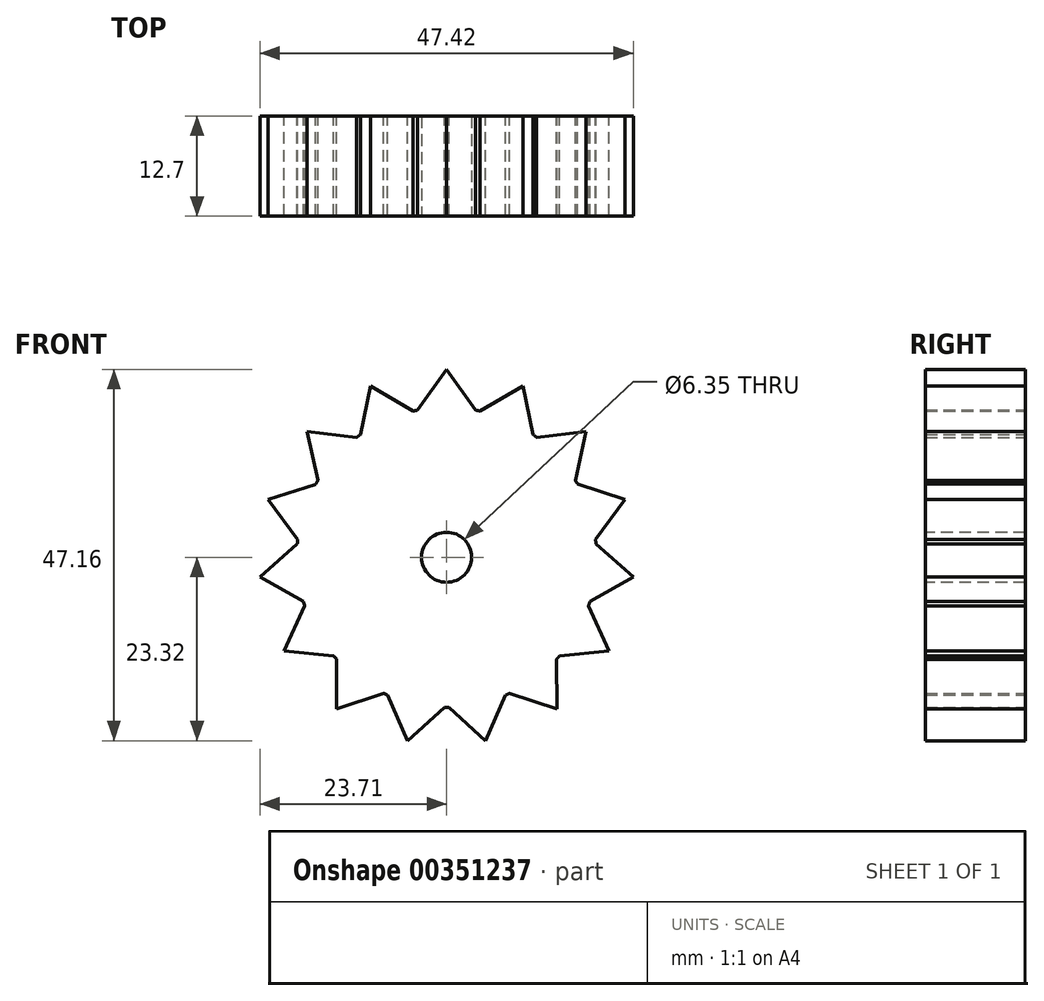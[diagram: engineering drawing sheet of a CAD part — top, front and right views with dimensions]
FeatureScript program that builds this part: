
annotation { "Feature Type Name" : "Feature", "Feature Type Description" : "" }
export const myFeature = defineFeature(function(context is Context, id is Id, definition is map)
    precondition{}
    {
        {
            var Q0;
            Q0=qCreatedBy(makeId("Front.planeOp"),FACE);
            var sketch = newSketch(context, id + "F0", { "sketchPlane" : qUnion([Q0])});
            skCircle(sketch, "E0", {"center": v(0, 0) * mm, "radius": 19.05 * mm});
            skPoint(sketch, "E1.start.orphan", {"position": v(0, 19.05) * mm});
            skLineSegment(sketch, "E2", {"start": v(0, 23.84) * mm, "end": v(3.68, 18.7) * mm});
            skLineSegment(sketch, "E3", {"start": v(0, 23.84) * mm, "end": v(-3.68, 18.7) * mm});
            skLineSegment(sketch, "E4.1.0", {"start": v(-9.7, 21.77) * mm, "end": v(-10.96, 15.58) * mm});
            skLineSegment(sketch, "E4.1.1", {"start": v(-9.7, 21.77) * mm, "end": v(-4.24, 18.57) * mm});
            skLineSegment(sketch, "E4.2.0", {"start": v(-17.71, 15.95) * mm, "end": v(-16.35, 9.77) * mm});
            skLineSegment(sketch, "E4.2.1", {"start": v(-17.71, 15.95) * mm, "end": v(-11.43, 15.24) * mm});
            skLineSegment(sketch, "E4.3.0", {"start": v(-22.67, 7.36) * mm, "end": v(-18.91, 2.28) * mm});
            skLineSegment(sketch, "E4.3.1", {"start": v(-22.67, 7.36) * mm, "end": v(-16.64, 9.27) * mm});
            skLineSegment(sketch, "E4.4.0", {"start": v(-23.7, -2.5) * mm, "end": v(-18.2, -5.61) * mm});
            skLineSegment(sketch, "E4.4.1", {"start": v(-23.7, -2.5) * mm, "end": v(-18.97, 1.7) * mm});
            skLineSegment(sketch, "E4.5.0", {"start": v(-20.64, -11.92) * mm, "end": v(-14.35, -12.53) * mm});
            skLineSegment(sketch, "E4.5.1", {"start": v(-20.64, -11.92) * mm, "end": v(-18.03, -6.16) * mm});
            skLineSegment(sketch, "E4.6.0", {"start": v(-14, -19.28) * mm, "end": v(-8, -17.28) * mm});
            skLineSegment(sketch, "E4.6.1", {"start": v(-14, -19.28) * mm, "end": v(-13.96, -12.96) * mm});
            skLineSegment(sketch, "E4.7.0", {"start": v(-4.95, -23.32) * mm, "end": v(-0.29, -19.05) * mm});
            skLineSegment(sketch, "E4.7.1", {"start": v(-4.95, -23.32) * mm, "end": v(-7.48, -17.52) * mm});
            skLineSegment(sketch, "E4.8.0", {"start": v(4.96, -23.31) * mm, "end": v(7.49, -17.52) * mm});
            skLineSegment(sketch, "E4.8.1", {"start": v(4.96, -23.31) * mm, "end": v(0.29, -19.05) * mm});
            skLineSegment(sketch, "E4.9.0", {"start": v(14.01, -19.28) * mm, "end": v(13.96, -12.96) * mm});
            skLineSegment(sketch, "E4.9.1", {"start": v(14.01, -19.28) * mm, "end": v(8.01, -17.28) * mm});
            skLineSegment(sketch, "E4.10.0", {"start": v(20.64, -11.92) * mm, "end": v(18.03, -6.16) * mm});
            skLineSegment(sketch, "E4.10.1", {"start": v(20.64, -11.92) * mm, "end": v(14.35, -12.53) * mm});
            skLineSegment(sketch, "E4.11.0", {"start": v(23.7, -2.5) * mm, "end": v(18.97, 1.7) * mm});
            skLineSegment(sketch, "E4.11.1", {"start": v(23.7, -2.5) * mm, "end": v(18.2, -5.61) * mm});
            skLineSegment(sketch, "E4.12.0", {"start": v(22.67, 7.37) * mm, "end": v(16.64, 9.28) * mm});
            skLineSegment(sketch, "E4.12.1", {"start": v(22.67, 7.37) * mm, "end": v(18.91, 2.28) * mm});
            skLineSegment(sketch, "E4.13.0", {"start": v(17.71, 15.95) * mm, "end": v(11.43, 15.24) * mm});
            skLineSegment(sketch, "E4.13.1", {"start": v(17.71, 15.95) * mm, "end": v(16.35, 9.77) * mm});
            skLineSegment(sketch, "E4.14.0", {"start": v(9.7, 21.78) * mm, "end": v(4.24, 18.57) * mm});
            skLineSegment(sketch, "E4.14.1", {"start": v(9.7, 21.78) * mm, "end": v(10.96, 15.58) * mm});
            skSolve(sketch);
        }
        {
            var Q0;
            {var subQ0=sQuery(id+"F0.wireOp",EDGE,"E3");Q0=makeQuery(id+"F0.imprint","IMPRINT",FACE,{"disambiguationData":[TD([[makeQuery(id+"F0.imprint","IMPRINT",EDGE,{"derivedFrom":subQ0}),1.0]])]});}
            var Q1;
            {var subQ0=sQuery(id+"F0.wireOp",EDGE,"E4.1.0");Q1=makeQuery(id+"F0.imprint","IMPRINT",FACE,{"disambiguationData":[TD([[makeQuery(id+"F0.imprint","IMPRINT",EDGE,{"derivedFrom":subQ0}),1.0]])]});}
            var Q2;
            {var subQ0=sQuery(id+"F0.wireOp",EDGE,"E4.2.0");Q2=makeQuery(id+"F0.imprint","IMPRINT",FACE,{"disambiguationData":[TD([[makeQuery(id+"F0.imprint","IMPRINT",EDGE,{"derivedFrom":subQ0}),1.0]])]});}
            var Q3;
            {var subQ0=sQuery(id+"F0.wireOp",EDGE,"E4.3.0");Q3=makeQuery(id+"F0.imprint","IMPRINT",FACE,{"disambiguationData":[TD([[makeQuery(id+"F0.imprint","IMPRINT",EDGE,{"derivedFrom":subQ0}),1.0]])]});}
            var Q4;
            {var subQ0=sQuery(id+"F0.wireOp",EDGE,"E4.14.0");Q4=makeQuery(id+"F0.imprint","IMPRINT",FACE,{"disambiguationData":[TD([[makeQuery(id+"F0.imprint","IMPRINT",EDGE,{"derivedFrom":subQ0}),1.0]])]});}
            var Q5;
            {var subQ0=sQuery(id+"F0.wireOp",EDGE,"E4.13.0");Q5=makeQuery(id+"F0.imprint","IMPRINT",FACE,{"disambiguationData":[TD([[makeQuery(id+"F0.imprint","IMPRINT",EDGE,{"derivedFrom":subQ0}),1.0]])]});}
            var Q6;
            {var subQ0=sQuery(id+"F0.wireOp",EDGE,"E4.12.0");Q6=makeQuery(id+"F0.imprint","IMPRINT",FACE,{"disambiguationData":[TD([[makeQuery(id+"F0.imprint","IMPRINT",EDGE,{"derivedFrom":subQ0}),1.0]])]});}
            var Q7;
            {var subQ0=sQuery(id+"F0.wireOp",EDGE,"E4.11.0");Q7=makeQuery(id+"F0.imprint","IMPRINT",FACE,{"disambiguationData":[TD([[makeQuery(id+"F0.imprint","IMPRINT",EDGE,{"derivedFrom":subQ0}),1.0]])]});}
            var Q8;
            {var subQ0=sQuery(id+"F0.wireOp",EDGE,"E4.10.0");Q8=makeQuery(id+"F0.imprint","IMPRINT",FACE,{"disambiguationData":[TD([[makeQuery(id+"F0.imprint","IMPRINT",EDGE,{"derivedFrom":subQ0}),1.0]])]});}
            var Q9;
            {var subQ0=sQuery(id+"F0.wireOp",EDGE,"E4.9.0");Q9=makeQuery(id+"F0.imprint","IMPRINT",FACE,{"disambiguationData":[TD([[makeQuery(id+"F0.imprint","IMPRINT",EDGE,{"derivedFrom":subQ0}),1.0]])]});}
            var Q10;
            {var subQ0=sQuery(id+"F0.wireOp",EDGE,"E0");var subQ18=makeQuery(id+"F0.imprint","INTERSECT",VERTEX,{"derivedFrom":[subQ0,sQuery(id+"F0.wireOp",EDGE,"E4.11.0")]});Q10=makeQuery(id+"F0.imprint","IMPRINT",FACE,{"disambiguationData":[TD([[makeQuery(id+"F0.imprint","IMPRINT",EDGE,{"disambiguationData":[TD([[subQ18,-1.0]])],"derivedFrom":subQ0}),1.0]])]});}
            var Q11;
            {var subQ0=sQuery(id+"F0.wireOp",EDGE,"E4.8.0");Q11=makeQuery(id+"F0.imprint","IMPRINT",FACE,{"disambiguationData":[TD([[makeQuery(id+"F0.imprint","IMPRINT",EDGE,{"derivedFrom":subQ0}),1.0]])]});}
            var Q12;
            {var subQ0=sQuery(id+"F0.wireOp",EDGE,"E4.7.0");Q12=makeQuery(id+"F0.imprint","IMPRINT",FACE,{"disambiguationData":[TD([[makeQuery(id+"F0.imprint","IMPRINT",EDGE,{"derivedFrom":subQ0}),1.0]])]});}
            var Q13;
            {var subQ0=sQuery(id+"F0.wireOp",EDGE,"E4.6.0");Q13=makeQuery(id+"F0.imprint","IMPRINT",FACE,{"disambiguationData":[TD([[makeQuery(id+"F0.imprint","IMPRINT",EDGE,{"derivedFrom":subQ0}),1.0]])]});}
            var Q14;
            {var subQ0=sQuery(id+"F0.wireOp",EDGE,"E4.5.0");Q14=makeQuery(id+"F0.imprint","IMPRINT",FACE,{"disambiguationData":[TD([[makeQuery(id+"F0.imprint","IMPRINT",EDGE,{"derivedFrom":subQ0}),1.0]])]});}
            var Q15;
            {var subQ0=sQuery(id+"F0.wireOp",EDGE,"E4.4.0");Q15=makeQuery(id+"F0.imprint","IMPRINT",FACE,{"disambiguationData":[TD([[makeQuery(id+"F0.imprint","IMPRINT",EDGE,{"derivedFrom":subQ0}),1.0]])]});}
            extrude(context, id + "F1", {"entities" : qUnion([Q0, Q1, Q2, Q3, Q4, Q5, Q6, Q7, Q8, Q9, Q10, Q11, Q12, Q13, Q14, Q15]), "depth" : 12.7 * mm});
        }
        {
            var Q0;
            Q0=makeQuery(id+"F1.opExtrude","CAP_FACE",FACE,{"disambiguationData":[OSD([sQuery(id+"F0.wireOp",EDGE,"E0")])],"isStart":false});
            var sketch = newSketch(context, id + "F2", { "sketchPlane" : qUnion([Q0])});
            skCircle(sketch, "E5", {"center": v(0, 0) * mm, "radius": 3.18 * mm});
            skSolve(sketch);
        }
        {
            var Q0;
            Q0=makeQuery(id+"F2.imprint","IMPRINT",FACE,{"disambiguationData":[TD([[makeQuery(id+"F2.imprint","IMPRINT",EDGE,{"derivedFrom":sQuery(id+"F2.wireOp",EDGE,"E5")}),1.0]])]});
            extrude(context, id + "F3", {"entities" : qUnion([Q0]), "operationType" : NewBodyOperationType.REMOVE, "oppositeDirection" : true, "depth" : 12.7 * mm});
        }
    });
